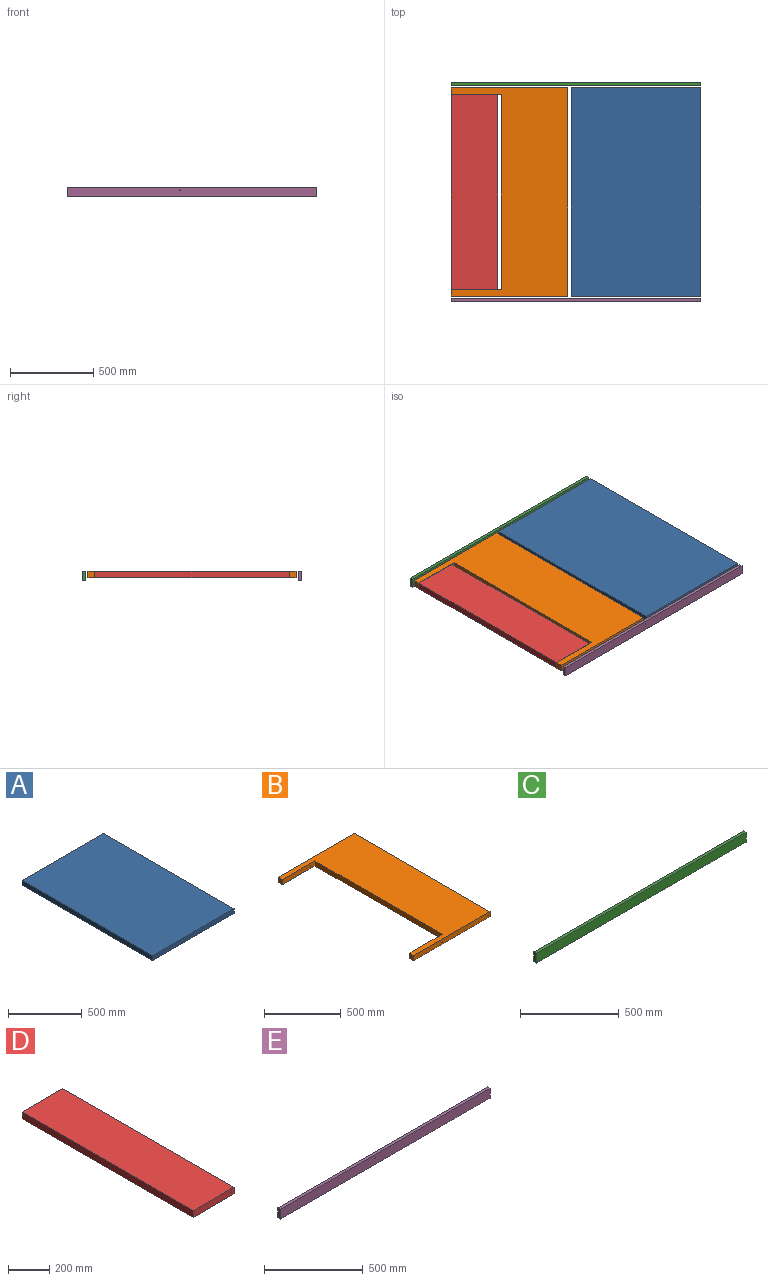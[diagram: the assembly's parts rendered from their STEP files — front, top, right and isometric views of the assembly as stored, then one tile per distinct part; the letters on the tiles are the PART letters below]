
ASSEMBLY  parts=5 mates=4
PART A: 6 faces, bbox 780x1250x40 mm
  f0: plane 780x40mm, normal (0,-1,0), area 31200mm2, adj f1,f3,f4,f5
  f1: plane 1250x40mm, normal (1,0,0), area 50000mm2, adj f0,f2,f4,f5
  f2: plane 780x40mm, normal (0,1,0), area 31200mm2, adj f1,f3,f4,f5
  f3: plane 1250x40mm, normal (-1,0,0), area 50000mm2, adj f0,f2,f4,f5
  f4: plane 1250x780mm, normal (0,0,1), area 975000mm2, adj f0,f1,f2,f3
  f5: plane 1250x780mm, normal (0,0,-1), area 975000mm2, adj f0,f1,f2,f3
PART B: 13 faces, bbox 700x1250x40 mm
  f0: plane 1250x40mm, normal (1,0,0), area 50000mm2, adj f1,f7,f8,f9
  f1: plane 700x40mm, normal (0,1,0), area 27960.7mm2, adj f0,f2,f8,f9,f11,f12
  f2: plane 40x40mm, normal (-1,0,0), area 1600mm2, adj f1,f3,f8,f9
  f3: plane 300x40mm, normal (0,-1,0), area 11980.4mm2, adj f2,f4,f8,f9,f12
  f4: plane 1170x40mm, normal (-1,0,0), area 46800mm2, adj f3,f5,f8,f9
  f5: plane 300x40mm, normal (0,1,0), area 11980.4mm2, adj f4,f6,f8,f9,f10
  f6: plane 40x40mm, normal (-1,0,0), area 1600mm2, adj f5,f7,f8,f9
  f7: plane 700x40mm, normal (0,-1,0), area 27960.7mm2, adj f0,f6,f8,f9,f10,f11
  f8: plane 1250x700mm, normal (0,0,1), area 524000mm2, adj f0,f1,f2,f3,f4,f5,f6,f7
  f9: plane 1250x700mm, normal (0,0,-1), area 524000mm2, adj f0,f1,f2,f3,f4,f5,f6,f7
  f10: cylinder r=2.5mm len=40mm, axis (0,-1,0), area 628.3mm2, adj f5,f7
  f11: cylinder r=2.5mm len=1250mm, axis (0,-1,0), area 19635mm2, adj f1,f7
  f12: cylinder r=2.5mm len=40mm, axis (0,-1,0), area 628.3mm2, adj f1,f3
PART C: 6 faces, bbox 1500x20x60 mm
  f0: plane 1500x60mm, normal (0,1,0), area 90000mm2, adj f1,f3,f4,f5
  f1: plane 60x20mm, normal (-1,0,0), area 1200mm2, adj f0,f2,f4,f5
  f2: plane 1500x60mm, normal (0,-1,0), area 90000mm2, adj f1,f3,f4,f5
  f3: plane 60x20mm, normal (1,0,0), area 1200mm2, adj f0,f2,f4,f5
  f4: plane 1500x20mm, normal (0,0,1), area 30000mm2, adj f0,f1,f2,f3
  f5: plane 1500x20mm, normal (0,0,-1), area 30000mm2, adj f0,f1,f2,f3
PART D: 7 faces, bbox 280x1170x40 mm
  f0: plane 1170x40mm, normal (-1,0,0), area 46800mm2, adj f1,f3,f4,f5
  f1: plane 280x40mm, normal (0,-1,0), area 11180.4mm2, adj f0,f2,f4,f5,f6
  f2: plane 1170x40mm, normal (1,0,0), area 46800mm2, adj f1,f3,f4,f5
  f3: plane 280x40mm, normal (0,1,0), area 11180.4mm2, adj f0,f2,f4,f5,f6
  f4: plane 1170x280mm, normal (0,0,1), area 327600mm2, adj f0,f1,f2,f3
  f5: plane 1170x280mm, normal (0,0,-1), area 327600mm2, adj f0,f1,f2,f3
  f6: cylinder r=2.5mm len=1170mm, axis (0,-1,0), area 18378.3mm2, adj f1,f3
PART E: 7 faces, bbox 1500x20x60 mm
  f0: plane 60x20mm, normal (-1,0,0), area 1200mm2, adj f1,f3,f4,f5
  f1: plane 1500x60mm, normal (0,-1,0), area 89980.4mm2, adj f0,f2,f4,f5,f6
  f2: plane 60x20mm, normal (1,0,0), area 1200mm2, adj f1,f3,f4,f5
  f3: plane 1500x60mm, normal (0,1,0), area 89980.4mm2, adj f0,f2,f4,f5,f6
  f4: plane 1500x20mm, normal (0,0,1), area 30000mm2, adj f0,f1,f2,f3
  f5: plane 1500x20mm, normal (0,0,-1), area 30000mm2, adj f0,f1,f2,f3
  f6: cylinder r=2.5mm len=20mm, axis (0,1,0), area 314.2mm2, adj f1,f3
PLACE A t=(169.7,371.28,270.67)mm
PLACE B t=(169.7,371.28,270.67)mm
PLACE C t=(169.7,371.28,270.67)mm
PLACE D t=(169.7,371.28,270.67)mm
PLACE E t=(169.7,371.28,270.67)mm
MATE fastened E.f2 <-> A.f1  axis (1,0,0) through (1669.7,391.28,330.67)mm
MATE revolute B.f11 <-> E.f6  axis (0,-1,0) through (849.7,406.28,310.67)mm
MATE revolute D.f6 <-> B.f10  axis (0,-1,0) through (429.7,446.28,310.67)mm
MATE fastened E.f2 <-> C.f3  axis (1,0,0) through (1669.7,381.28,300.67)mm
